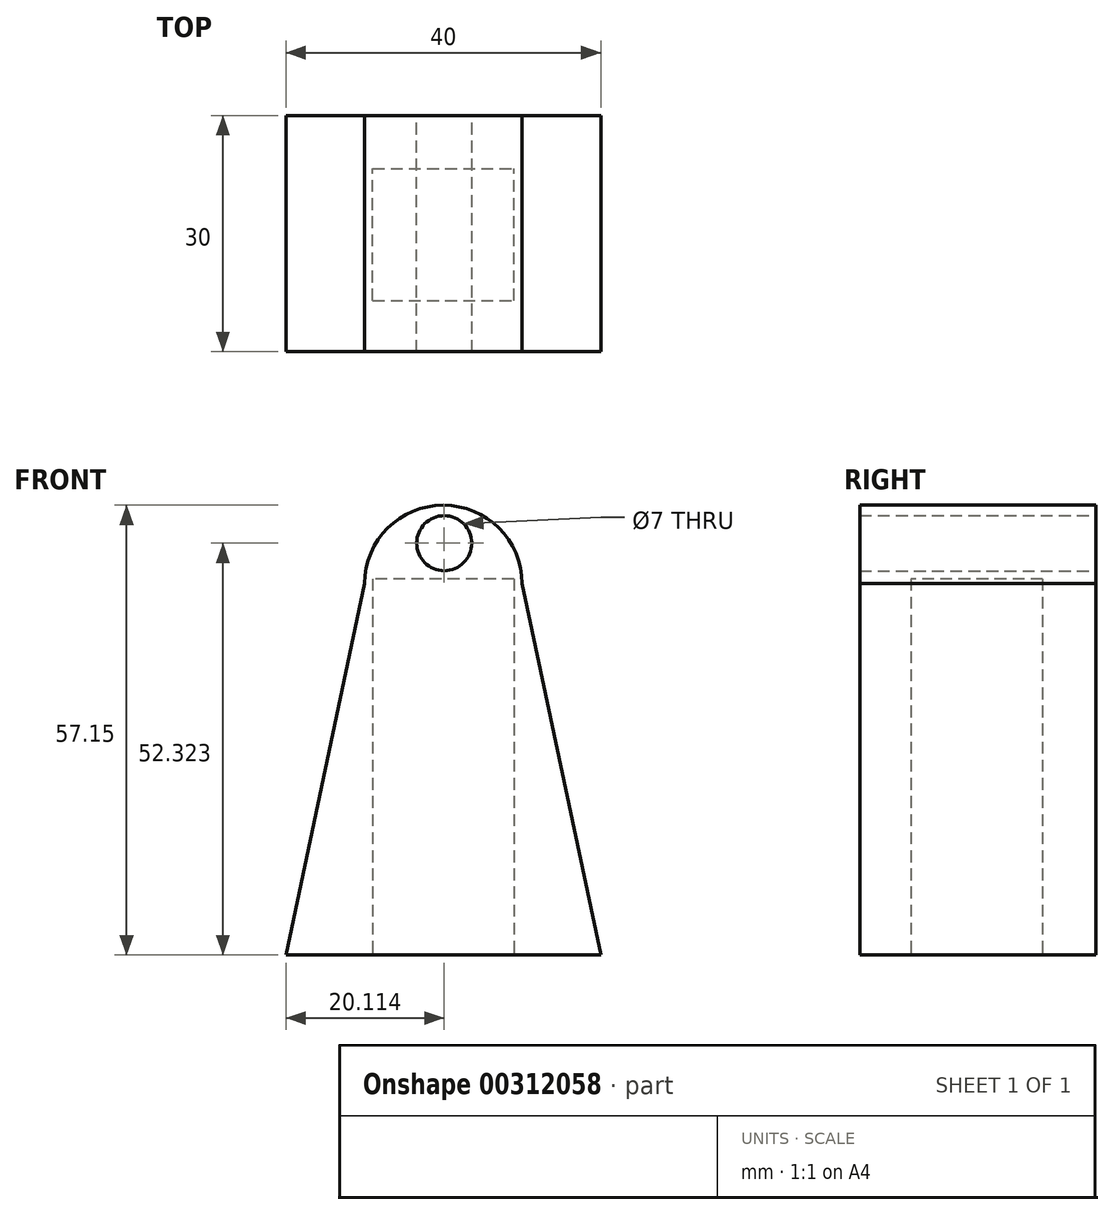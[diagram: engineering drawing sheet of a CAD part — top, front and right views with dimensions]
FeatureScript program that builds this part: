
annotation { "Feature Type Name" : "Feature", "Feature Type Description" : "" }
export const myFeature = defineFeature(function(context is Context, id is Id, definition is map)
    precondition{}
    {
        {
            var Q0;
            Q0=qCreatedBy(makeId("Front.planeOp"),FACE);
            var sketch = newSketch(context, id + "F0", { "sketchPlane" : qUnion([Q0])});
            skLineSegment(sketch, "E0", {"start": v(0, 0) * mm, "end": v(40, 0) * mm});
            skPoint(sketch, "E1.endSnap0", {"position": v(20, 0) * mm});
            skLineSegment(sketch, "E2", {"start": v(20, 0) * mm, "end": v(20, 51.24) * mm, "construction": true});
            skLineSegment(sketch, "E3", {"start": v(20, 47.19) * mm, "end": v(30, 47.19) * mm});
            skLineSegment(sketch, "E4", {"start": v(20, 47.19) * mm, "end": v(10, 47.19) * mm});
            skLineSegment(sketch, "E5", {"start": v(10, 47.19) * mm, "end": v(0, 0) * mm});
            skLineSegment(sketch, "E6", {"start": v(30, 47.19) * mm, "end": v(40, 0) * mm});
            skArc(sketch, "E7", {"start": v(30, 47.19) * mm, "mid": v(20, 57.15) * mm, "end": v(10, 47.19) * mm});
            skSolve(sketch);
        }
        {
            var Q0;
            Q0 = qSketchRegion(id + "F0", true);
            extrude(context, id + "F1", {"entities" : qUnion([Q0]), "depth" : 30 * mm});
        }
        {
            var Q0;
            Q0=qCreatedBy(makeId("Top.planeOp"),FACE);
            var sketch = newSketch(context, id + "F2", { "sketchPlane" : qUnion([Q0])});
            skPoint(sketch, "E8.middle", {"position": v(20, -15.13) * mm});
            skLineSegment(sketch, "E9.bottom", {"start": v(28.96, -6.77) * mm, "end": v(11.04, -6.77) * mm});
            skLineSegment(sketch, "E9.top", {"start": v(28.96, -23.5) * mm, "end": v(11.04, -23.5) * mm});
            skLineSegment(sketch, "E9.left", {"start": v(28.96, -6.77) * mm, "end": v(28.96, -23.5) * mm});
            skLineSegment(sketch, "E9.right", {"start": v(11.04, -6.77) * mm, "end": v(11.04, -23.5) * mm});
            skSolve(sketch);
        }
        {
            var Q0;
            Q0 = qSketchRegion(id + "F2", true);
            extrude(context, id + "F3", {"entities" : qUnion([Q0]), "operationType" : NewBodyOperationType.REMOVE, "endBound" : BoundingType.SYMMETRIC, "depth" : 95.6 * mm});
        }
        {
            var Q0;
            Q0=makeQuery(id+"F1.opExtrude","CAP_FACE",FACE,{"disambiguationData":[OSD([sQuery(id+"F0.wireOp",EDGE,"E0"),sQuery(id+"F0.wireOp",EDGE,"E5"),sQuery(id+"F0.wireOp",EDGE,"E6"),sQuery(id+"F0.wireOp",EDGE,"E7")])],"isStart":true});
            var sketch = newSketch(context, id + "F4", { "sketchPlane" : qUnion([Q0])});
            skCircle(sketch, "E10", {"center": v(-20.11, 52.32) * mm, "radius": 1.48 * mm});
            skSolve(sketch);
        }
        {
            var Q0;
            Q0=sQuery(id+"F4.wireOp",VERTEX,"E10.center");
            var Q1;
            Q1=makeQuery(id+"F1.opExtrude","SWEPT_BODY",BODY,{"disambiguationData":[OSD([sQuery(id+"F0.wireOp",EDGE,"E0"),sQuery(id+"F0.wireOp",EDGE,"E5"),sQuery(id+"F0.wireOp",EDGE,"E6"),sQuery(id+"F0.wireOp",EDGE,"E7")])]});
            hole(context, id + "F5", {"style" : HoleStyle.SIMPLE, "endStyle" : HoleEndStyle.THROUGH, "standardTappedOrClearance" : lookupTablePath({ "standard" : "ISO", "engagement" : "75%", "pitch" : "1 mm", "size" : "M8", "type" : "Tapped" }), "standardBlindInLast" : lookupTablePath({ "standard" : "ISO", "engagement" : "75%", "pitch" : "1 mm", "size" : "M8", "type" : "Tapped" }), "holeDiameter" : 7 * mm, "showTappedDepth" : true, "tappedDepth" : 6 * mm, "tapClearance" : 3, "locations" : qUnion([Q0]), "scope" : qUnion([Q1]), "majorDiameter" : 8 * mm});
        }
    });
